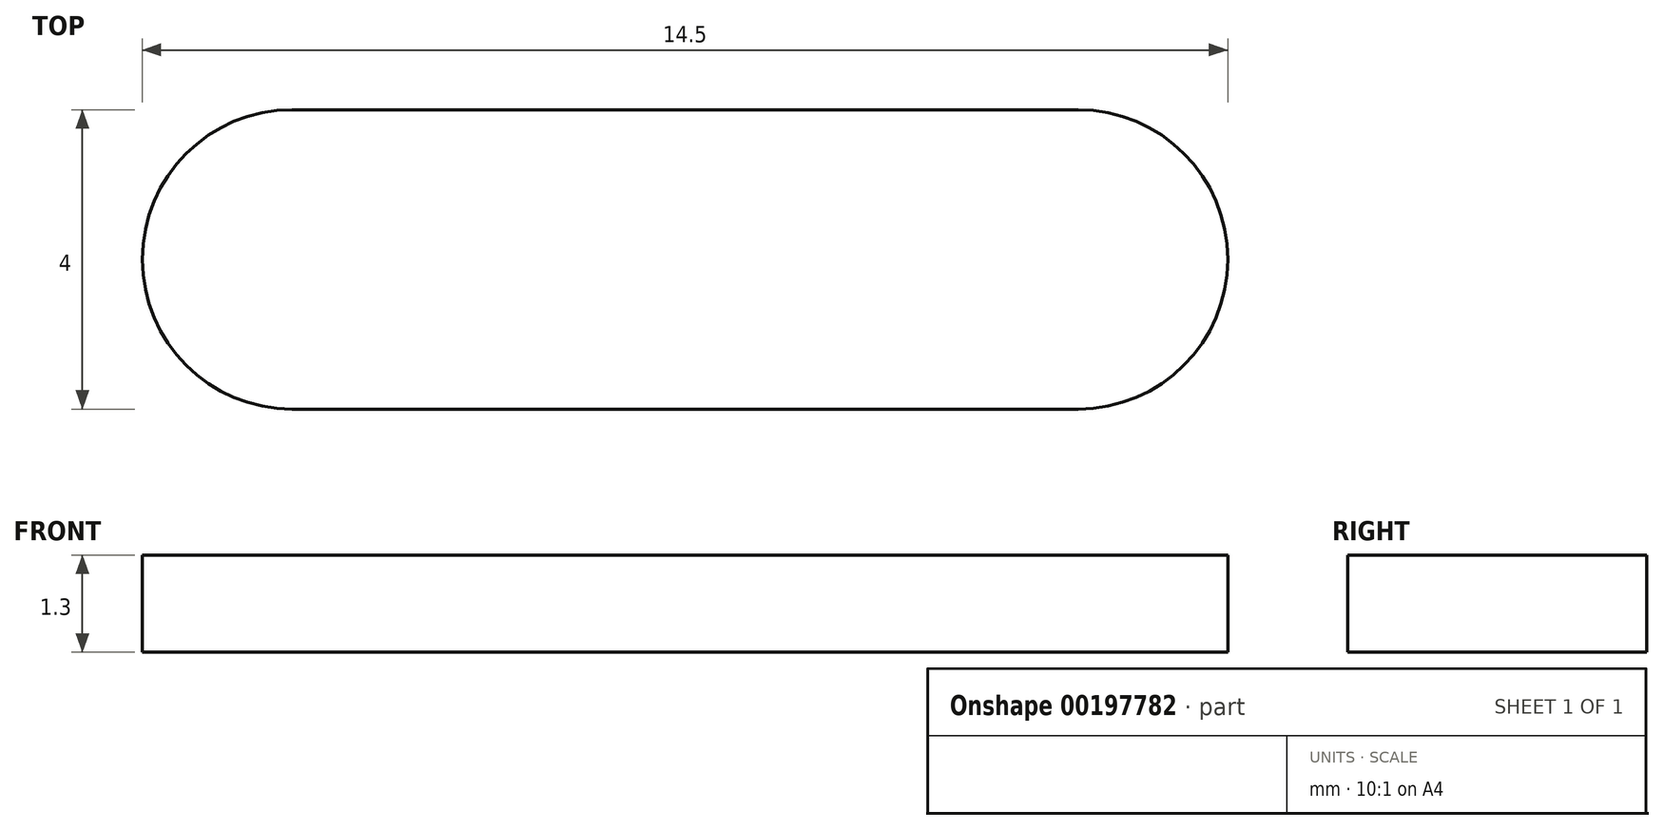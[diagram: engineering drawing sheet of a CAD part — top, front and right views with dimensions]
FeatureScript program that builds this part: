
annotation { "Feature Type Name" : "Feature", "Feature Type Description" : "" }
export const myFeature = defineFeature(function(context is Context, id is Id, definition is map)
    precondition{}
    {
        {
            var Q0;
            Q0=qCreatedBy(makeId("Top.planeOp"),FACE);
            var sketch = newSketch(context, id + "F0", { "sketchPlane" : qUnion([Q0])});
            skLineSegment(sketch, "E0.bottom", {"start": v(5.25, -2) * mm, "end": v(-5.25, -2) * mm});
            skLineSegment(sketch, "E0.top", {"start": v(5.25, 2) * mm, "end": v(-5.25, 2) * mm});
            skLineSegment(sketch, "E0.left", {"start": v(5.25, -2) * mm, "end": v(5.25, 2) * mm});
            skLineSegment(sketch, "E0.right", {"start": v(-5.25, -2) * mm, "end": v(-5.25, 2) * mm});
            skPoint(sketch, "E0.middle", {"position": v(0, 0) * mm});
            skArc(sketch, "E1", {"start": v(-5.25, 2) * mm, "mid": v(-7.25, 0) * mm, "end": v(-5.25, -2) * mm});
            skArc(sketch, "E2", {"start": v(5.25, -2) * mm, "mid": v(7.25, 0) * mm, "end": v(5.25, 2) * mm});
            skSolve(sketch);
        }
        {
            var Q0;
            Q0 = qSketchRegion(id + "F0", true);
            extrude(context, id + "F1", {"entities" : qUnion([Q0]), "depth" : 1.3 * mm});
        }
    });
